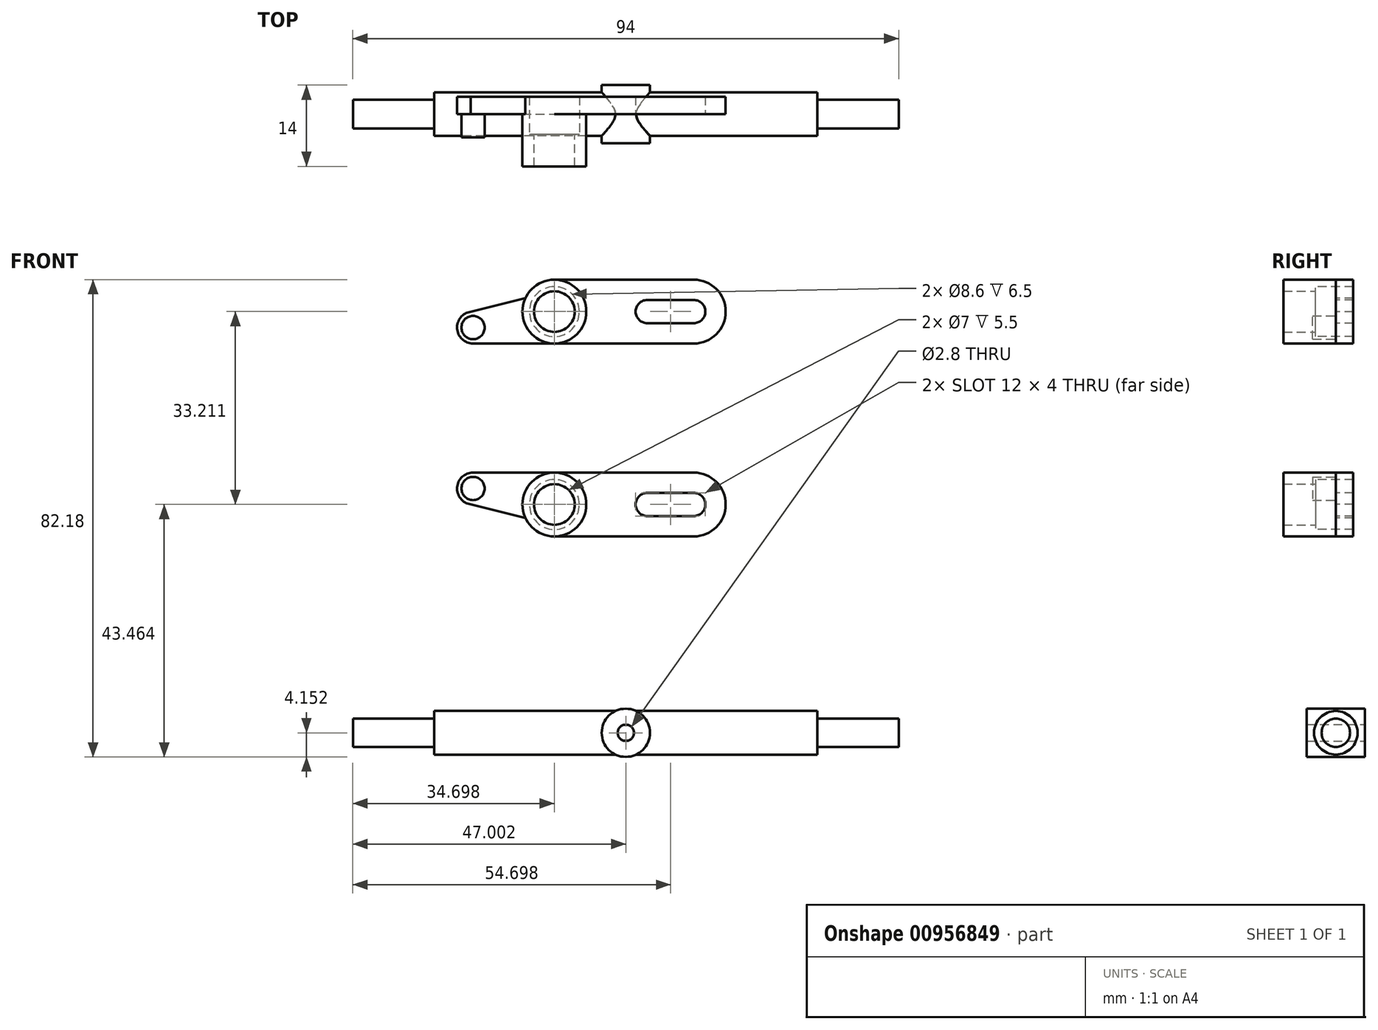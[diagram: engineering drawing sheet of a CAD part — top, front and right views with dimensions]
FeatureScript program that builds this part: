
annotation { "Feature Type Name" : "Feature", "Feature Type Description" : "" }
export const myFeature = defineFeature(function(context is Context, id is Id, definition is map)
    precondition{}
    {
        {
            var Q0;
            Q0=qCreatedBy(makeId("Front.planeOp"),FACE);
            var sketch = newSketch(context, id + "F0", { "sketchPlane" : qUnion([Q0])});
            skLineSegment(sketch, "E0.bottom", {"start": v(-5.5, 22.1) * mm, "end": v(18.5, 22.1) * mm});
            skLineSegment(sketch, "E0.top", {"start": v(-5.5, 11.1) * mm, "end": v(18.5, 11.1) * mm});
            skLineSegment(sketch, "E1", {"start": v(-11, 16.6) * mm, "end": v(-5.5, 16.6) * mm, "construction": true});
            skLineSegment(sketch, "E2", {"start": v(24, 16.6) * mm, "end": v(18.5, 16.6) * mm, "construction": true});
            skCircle(sketch, "E3", {"center": v(-5.5, 16.6) * mm, "radius": 5.5 * mm});
            skArc(sketch, "E4", {"start": v(18.5, 11.1) * mm, "mid": v(24, 16.6) * mm, "end": v(18.5, 22.1) * mm});
            skArc(sketch, "E5", {"start": v(18.5, 14.6) * mm, "mid": v(20.5, 16.6) * mm, "end": v(18.5, 18.6) * mm});
            skLineSegment(sketch, "E6", {"start": v(18.5, 16.6) * mm, "end": v(10.5, 16.6) * mm, "construction": true});
            skArc(sketch, "E7", {"start": v(10.5, 18.6) * mm, "mid": v(8.5, 16.6) * mm, "end": v(10.5, 14.6) * mm});
            skLineSegment(sketch, "E8", {"start": v(10.5, 16.6) * mm, "end": v(10.5, 20.66) * mm, "construction": true});
            skLineSegment(sketch, "E9", {"start": v(10.5, 16.6) * mm, "end": v(10.5, 12.53) * mm, "construction": true});
            skLineSegment(sketch, "E10", {"start": v(18.5, 16.6) * mm, "end": v(18.5, 20.94) * mm, "construction": true});
            skLineSegment(sketch, "E11", {"start": v(18.5, 16.6) * mm, "end": v(18.5, 12.74) * mm, "construction": true});
            skLineSegment(sketch, "E12", {"start": v(10.5, 18.6) * mm, "end": v(18.5, 18.6) * mm});
            skLineSegment(sketch, "E13", {"start": v(10.5, 14.6) * mm, "end": v(18.5, 14.6) * mm});
            skLineSegment(sketch, "E14", {"start": v(-5.5, 11.1) * mm, "end": v(-19.5, 11.1) * mm});
            skLineSegment(sketch, "E15", {"start": v(-19.5, 11.1) * mm, "end": v(-19.5, 13.86) * mm, "construction": true});
            skCircle(sketch, "E16", {"center": v(-19.5, 13.86) * mm, "radius": 2.75 * mm});
            skLineSegment(sketch, "E17", {"start": v(-19.88, 16.58) * mm, "end": v(-10.49, 18.93) * mm});
            skCircle(sketch, "E18", {"center": v(-19.5, 13.86) * mm, "radius": 2 * mm});
            skCircle(sketch, "E19", {"center": v(-5.5, 16.6) * mm, "radius": 3.5 * mm});
            skCircle(sketch, "E20", {"center": v(-5.5, 16.6) * mm, "radius": 4.3 * mm});
            skSolve(sketch);
        }
        {
            var Q0;
            {var subQ0=sQuery(id+"F0.wireOp",EDGE,"E14");Q0=makeQuery(id+"F0.imprint","IMPRINT",FACE,{"disambiguationData":[TD([[makeQuery(id+"F0.imprint","IMPRINT",EDGE,{"derivedFrom":subQ0}),-1.0]])]});}
            var Q1;
            {var subQ0=sQuery(id+"F0.wireOp",EDGE,"E3");var subQ1=makeQuery(id+"F0.imprint","INTERSECT",VERTEX,{"derivedFrom":[sQuery(id+"F0.wireOp",EDGE,"E0.bottom"),subQ0]});Q1=makeQuery(id+"F0.imprint","IMPRINT",FACE,{"disambiguationData":[TD([[makeQuery(id+"F0.imprint","IMPRINT",EDGE,{"disambiguationData":[TD([[subQ1,-1.0]])],"derivedFrom":subQ0}),1.0]])]});}
            var Q2;
            {var subQ1=sQuery(id+"F0.wireOp",EDGE,"E0.bottom");Q2=makeQuery(id+"F0.imprint","IMPRINT",FACE,{"disambiguationData":[TD([[makeQuery(id+"F0.imprint","IMPRINT",EDGE,{"derivedFrom":subQ1}),-1.0]])]});}
            var Q3;
            Q3=makeQuery(id+"F0.imprint","IMPRINT",FACE,{"disambiguationData":[TD([[makeQuery(id+"F0.imprint","IMPRINT",EDGE,{"derivedFrom":sQuery(id+"F0.wireOp",EDGE,"E18")}),-1.0]])]});
            var Q4;
            Q4=makeQuery(id+"F0.imprint","IMPRINT",FACE,{"disambiguationData":[TD([[makeQuery(id+"F0.imprint","IMPRINT",EDGE,{"derivedFrom":sQuery(id+"F0.wireOp",EDGE,"E18")}),1.0]])]});
            extrude(context, id + "F1", {"entities" : qUnion([Q0, Q1, Q2, Q3, Q4]), "oppositeDirection" : true, "depth" : 3 * mm, "offsetDistance" : 25 * mm});
        }
        {
            var Q0;
            Q0=makeQuery(id+"F0.imprint","IMPRINT",FACE,{"disambiguationData":[TD([[makeQuery(id+"F0.imprint","IMPRINT",EDGE,{"derivedFrom":sQuery(id+"F0.wireOp",EDGE,"E18")}),1.0]])]});
            extrude(context, id + "F2", {"entities" : qUnion([Q0]), "operationType" : NewBodyOperationType.ADD, "depth" : 4 * mm, "offsetDistance" : 25 * mm});
        }
        {
            var Q0;
            {var subQ0=sQuery(id+"F0.wireOp",EDGE,"E3");var subQ1=makeQuery(id+"F0.imprint","INTERSECT",VERTEX,{"derivedFrom":[sQuery(id+"F0.wireOp",EDGE,"E0.bottom"),subQ0]});Q0=makeQuery(id+"F0.imprint","IMPRINT",FACE,{"disambiguationData":[TD([[makeQuery(id+"F0.imprint","IMPRINT",EDGE,{"disambiguationData":[TD([[subQ1,-1.0]])],"derivedFrom":subQ0}),1.0]])]});}
            var Q1;
            Q1=makeQuery(id+"F0.imprint","IMPRINT",FACE,{"disambiguationData":[TD([[makeQuery(id+"F0.imprint","IMPRINT",EDGE,{"derivedFrom":sQuery(id+"F0.wireOp",EDGE,"E19")}),-1.0]])]});
            extrude(context, id + "F3", {"entities" : qUnion([Q0, Q1]), "operationType" : NewBodyOperationType.ADD, "depth" : 9 * mm, "offsetDistance" : 25 * mm});
        }
        {
            var Q0;
            Q0=makeQuery(id+"F3.opExtrude","CAP_FACE",FACE,{"disambiguationData":[OSD([sQuery(id+"F0.wireOp",EDGE,"E3"),sQuery(id+"F0.wireOp",EDGE,"E19")])],"isStart":true});
            var Q1;
            Q1=sQuery(id+"F0.wireOp",EDGE,"E20");
            var Q2;
            Q2=sQuery(id+"F0.wireOp",EDGE,"E19");
            extrude(context, id + "F4", {"entities" : qUnion([Q0]), "operationType" : NewBodyOperationType.REMOVE, "surfaceEntities" : qUnion([Q1, Q2]), "oppositeDirection" : true, "depth" : 3.5 * mm, "offsetDistance" : 25 * mm});
        }
        {
            var Q0;
            Q0=makeQuery(id+"F1.opExtrude","SWEPT_BODY",BODY,{"disambiguationData":[OSD([sQuery(id+"F0.wireOp",EDGE,"E0.bottom"),sQuery(id+"F0.wireOp",EDGE,"E0.top"),sQuery(id+"F0.wireOp",EDGE,"E3"),sQuery(id+"F0.wireOp",EDGE,"E4"),sQuery(id+"F0.wireOp",EDGE,"E5"),sQuery(id+"F0.wireOp",EDGE,"E7"),sQuery(id+"F0.wireOp",EDGE,"E12"),sQuery(id+"F0.wireOp",EDGE,"E13"),sQuery(id+"F0.wireOp",EDGE,"E14"),sQuery(id+"F0.wireOp",EDGE,"E16"),sQuery(id+"F0.wireOp",EDGE,"E17"),sQuery(id+"F0.wireOp",EDGE,"E20")])]});
            var Q1;
            Q1=qCreatedBy(makeId("Top.planeOp"),FACE);
            mirror(context, id + "F5", {"entities" : qUnion([Q0]), "mirrorPlane" : qUnion([Q1])});
        }
        {
            var Q0;
            Q0=qCreatedBy(makeId("Front.planeOp"),FACE);
            var sketch = newSketch(context, id + "F6", { "sketchPlane" : qUnion([Q0])});
            skLineSegment(sketch, "E21", {"start": v(-31.7, -55.92) * mm, "end": v(2.65, -55.92) * mm, "construction": true});
            skLineSegment(sketch, "E22", {"start": v(6.8, -44.9) * mm, "end": v(6.8, -68.68) * mm, "construction": true});
            skCircle(sketch, "E23", {"center": v(6.8, -55.92) * mm, "radius": 4.15 * mm});
            skLineSegment(sketch, "E24", {"start": v(5.4, -55.92) * mm, "end": v(-26.2, -55.92) * mm, "construction": true});
            skLineSegment(sketch, "E25", {"start": v(-26.2, -55.92) * mm, "end": v(-26.2, -52.17) * mm});
            skLineSegment(sketch, "E26", {"start": v(-26.2, -52.17) * mm, "end": v(5.02, -52.17) * mm});
            skLineSegment(sketch, "E27", {"start": v(39.8, -52.17) * mm, "end": v(39.8, -59.67) * mm});
            skLineSegment(sketch, "E28", {"start": v(39.8, -59.67) * mm, "end": v(8.58, -59.67) * mm});
            skLineSegment(sketch, "E29", {"start": v(-26.2, -59.67) * mm, "end": v(-26.2, -55.92) * mm});
            skLineSegment(sketch, "E30", {"start": v(-26.2, -55.92) * mm, "end": v(-40.2, -55.92) * mm, "construction": true});
            skLineSegment(sketch, "E31", {"start": v(-40.2, -55.92) * mm, "end": v(-40.2, -53.47) * mm});
            skLineSegment(sketch, "E32", {"start": v(-40.2, -53.47) * mm, "end": v(-26.2, -53.47) * mm});
            skLineSegment(sketch, "E33", {"start": v(53.8, -53.47) * mm, "end": v(53.8, -58.37) * mm});
            skLineSegment(sketch, "E34", {"start": v(53.8, -58.37) * mm, "end": v(39.8, -58.37) * mm});
            skLineSegment(sketch, "E35", {"start": v(-40.2, -58.37) * mm, "end": v(-40.2, -55.92) * mm});
            skCircle(sketch, "E36", {"center": v(6.8, -55.92) * mm, "radius": 1.4 * mm});
            skLineSegment(sketch, "E37.trimOffspring", {"start": v(-26.2, -58.37) * mm, "end": v(-40.2, -58.37) * mm});
            skLineSegment(sketch, "E38.trimOffspring", {"start": v(5.02, -59.67) * mm, "end": v(-26.2, -59.67) * mm});
            skLineSegment(sketch, "E39.trimOffspring", {"start": v(5.4, -55.92) * mm, "end": v(8.2, -55.92) * mm, "construction": true});
            skLineSegment(sketch, "E40.trimOffspring", {"start": v(10.95, -55.92) * mm, "end": v(44.41, -55.92) * mm, "construction": true});
            skLineSegment(sketch, "E41.trimOffspring", {"start": v(39.8, -53.47) * mm, "end": v(53.8, -53.47) * mm});
            skLineSegment(sketch, "E42.trimOffspring", {"start": v(8.58, -52.17) * mm, "end": v(39.8, -52.17) * mm});
            skLineSegment(sketch, "E43", {"start": v(-40.2, -55.92) * mm, "end": v(53.8, -55.92) * mm});
            skSolve(sketch);
        }
        {
            var Q0;
            Q0=makeQuery(id+"F6.imprint","IMPRINT",FACE,{"disambiguationData":[TD([[makeQuery(id+"F6.imprint","IMPRINT",EDGE,{"derivedFrom":sQuery(id+"F6.wireOp",EDGE,"E36")}),-1.0]])]});
            var Q1;
            Q1=sQuery(id+"F6.wireOp",EDGE,"E23");
            var Q2;
            Q2=sQuery(id+"F6.wireOp",EDGE,"E36");
            extrude(context, id + "F7", {"entities" : qUnion([Q0]), "surfaceEntities" : qUnion([Q1, Q2]), "depth" : 5 * mm, "offsetDistance" : 25 * mm});
        }
        {
            var Q0;
            Q0=makeQuery(id+"F6.imprint","IMPRINT",FACE,{"disambiguationData":[TD([[makeQuery(id+"F6.imprint","IMPRINT",EDGE,{"derivedFrom":sQuery(id+"F6.wireOp",EDGE,"E36")}),-1.0]])]});
            extrude(context, id + "F8", {"entities" : qUnion([Q0]), "operationType" : NewBodyOperationType.ADD, "oppositeDirection" : true, "depth" : 5 * mm, "offsetDistance" : 25 * mm});
        }
        {
            var Q0;
            {var subQ0=sQuery(id+"F6.wireOp",EDGE,"E26");Q0=makeQuery(id+"F6.imprint","IMPRINT",FACE,{"disambiguationData":[TD([[makeQuery(id+"F6.imprint","IMPRINT",EDGE,{"derivedFrom":subQ0}),-1.0]])]});}
            var Q1;
            {var subQ4=sQuery(id+"F6.wireOp",EDGE,"E31");Q1=makeQuery(id+"F6.imprint","IMPRINT",FACE,{"disambiguationData":[TD([[makeQuery(id+"F6.imprint","IMPRINT",EDGE,{"derivedFrom":subQ4}),-1.0]])]});}
            var Q2;
            {var subQ0=sQuery(id+"F6.wireOp",EDGE,"E42.trimOffspring");Q2=makeQuery(id+"F6.imprint","IMPRINT",FACE,{"disambiguationData":[TD([[makeQuery(id+"F6.imprint","IMPRINT",EDGE,{"derivedFrom":subQ0}),-1.0]])]});}
            var Q3;
            {var subQ0=sQuery(id+"F6.wireOp",EDGE,"E41.trimOffspring");Q3=makeQuery(id+"F6.imprint","IMPRINT",FACE,{"disambiguationData":[TD([[makeQuery(id+"F6.imprint","IMPRINT",EDGE,{"derivedFrom":subQ0}),-1.0]])]});}
            var Q4;
            Q4=sQuery(id+"F6.wireOp",EDGE,"E26");
            var Q5;
            Q5=sQuery(id+"F6.wireOp",EDGE,"E32");
            var Q6;
            Q6=sQuery(id+"F6.wireOp",EDGE,"E25");
            var Q7;
            Q7=sQuery(id+"F6.wireOp",EDGE,"E31");
            var Q8;
            Q8=sQuery(id+"F6.wireOp",EDGE,"E42.trimOffspring");
            var Q9;
            Q9=sQuery(id+"F6.wireOp",EDGE,"E27");
            var Q10;
            Q10=sQuery(id+"F6.wireOp",EDGE,"E41.trimOffspring");
            var Q11;
            Q11=sQuery(id+"F6.wireOp",EDGE,"E33");
            var Q12;
            Q12=sQuery(id+"F6.wireOp",EDGE,"E34");
            var Q13;
            Q13=sQuery(id+"F6.wireOp",EDGE,"E28");
            var Q14;
            Q14=sQuery(id+"F6.wireOp",EDGE,"E38.trimOffspring");
            var Q15;
            Q15=sQuery(id+"F6.wireOp",EDGE,"E29");
            var Q16;
            Q16=sQuery(id+"F6.wireOp",EDGE,"E37.trimOffspring");
            var Q17;
            Q17=sQuery(id+"F6.wireOp",EDGE,"E35");
            var Q18;
            Q18=sQuery(id+"F6.wireOp",EDGE,"E43");
            revolve(context, id + "F9", {"operationType" : NewBodyOperationType.ADD, "surfaceOperationType" : NewSurfaceOperationType.ADD, "entities" : qUnion([Q0, Q1, Q2, Q3]), "surfaceEntities" : qUnion([Q4, Q5, Q6, Q7, Q8, Q9, Q10, Q11, Q12, Q13, Q14, Q15, Q16, Q17]), "axis" : qUnion([Q18]), "revolveType" : RevolveType.FULL});
        }
    });
